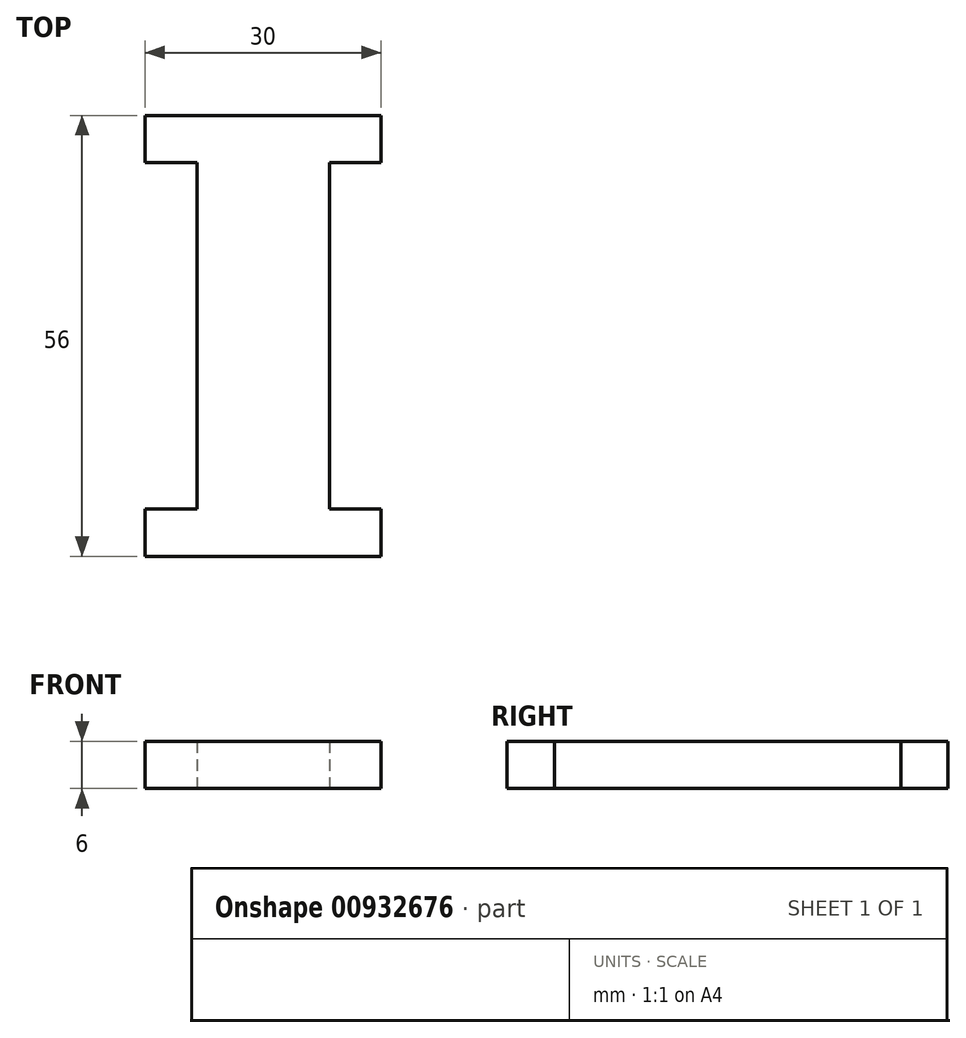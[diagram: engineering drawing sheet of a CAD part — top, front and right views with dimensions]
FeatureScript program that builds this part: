
annotation { "Feature Type Name" : "Feature", "Feature Type Description" : "" }
export const myFeature = defineFeature(function(context is Context, id is Id, definition is map)
    precondition{}
    {
        {
            var Q0;
            Q0=qCreatedBy(makeId("Top.planeOp"),FACE);
            var sketch = newSketch(context, id + "F0", { "sketchPlane" : qUnion([Q0])});
            skLineSegment(sketch, "E0.bottom", {"start": v(15, 28) * mm, "end": v(-15, 28) * mm});
            skLineSegment(sketch, "E0.top", {"start": v(15, -28) * mm, "end": v(-15, -28) * mm});
            skLineSegment(sketch, "E0.left", {"start": v(15, 28) * mm, "end": v(15, 22) * mm});
            skLineSegment(sketch, "E0.right", {"start": v(-15, 28) * mm, "end": v(-15, 22) * mm});
            skPoint(sketch, "E0.middle", {"position": v(0, 0) * mm});
            skLineSegment(sketch, "E1.bottom", {"start": v(15, 22) * mm, "end": v(8.4, 22) * mm});
            skLineSegment(sketch, "E1.top", {"start": v(15, -22) * mm, "end": v(8.4, -22) * mm});
            skLineSegment(sketch, "E1.right", {"start": v(8.4, 22) * mm, "end": v(8.4, -22) * mm});
            skLineSegment(sketch, "E2.bottom", {"start": v(-15, 22) * mm, "end": v(-8.4, 22) * mm});
            skLineSegment(sketch, "E2.top", {"start": v(-15, -22) * mm, "end": v(-8.4, -22) * mm});
            skLineSegment(sketch, "E2.right", {"start": v(-8.4, 22) * mm, "end": v(-8.4, -22) * mm});
            skLineSegment(sketch, "E3.trimOffspring", {"start": v(-15, -22) * mm, "end": v(-15, -28) * mm});
            skLineSegment(sketch, "E4.trimOffspring", {"start": v(15, -22) * mm, "end": v(15, -28) * mm});
            skSolve(sketch);
        }
        {
            var Q0;
            Q0=makeQuery(id+"F0.imprint","IMPRINT",FACE,{"disambiguationData":[TD([[makeQuery(id+"F0.imprint","IMPRINT",EDGE,{"derivedFrom":sQuery(id+"F0.wireOp",EDGE,"E0.bottom")}),1.0]])]});
            extrude(context, id + "F1", {"entities" : qUnion([Q0]), "depth" : 6 * mm, "offsetDistance" : 25 * mm});
        }
    });
